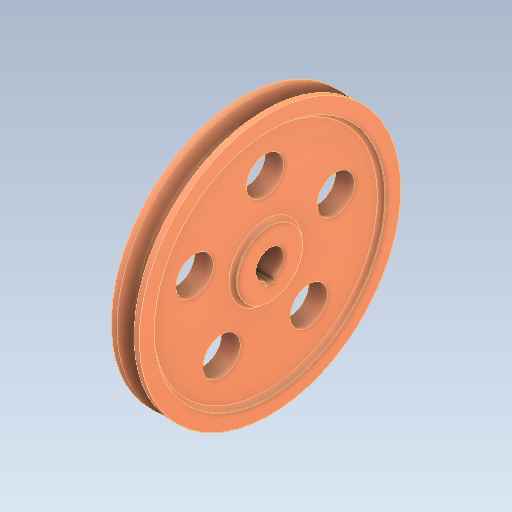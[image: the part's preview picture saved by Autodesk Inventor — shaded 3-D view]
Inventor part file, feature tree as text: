
AUTODESK INVENTOR PART (.ipt)
format: ipt  version: 2021 (Build 250183000, 183)  size: 219,648 bytes
history: mixed  units: mm
features: other x1, extrude x1, imported_body x1
ambient origin geometry x8: Origin, YZ Plane, XZ Plane, XY Plane, X Axis, Y Axis, Z Axis, Center Point
bodies: Body1 (imported_parasolid)
feature tree (3):
  other  "Sólido1"
  extrude  "Extrude2"  [1 undecoded]
  imported_body  NMx_Import_Brep_tag  [imported B-rep: ~28 faces, bbox_mm=[15.0, 77.786278, 104.714327]]
note: 1 required parameter value undecoded (feature->parameter linkage not recoverable at this tier; creation-order binding heuristic only, values carry confidence <= 0.55)
